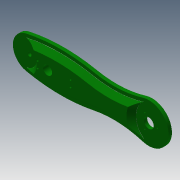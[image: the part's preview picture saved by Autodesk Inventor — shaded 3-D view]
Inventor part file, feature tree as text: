
AUTODESK INVENTOR PART (.ipt)
format: ipt  version: 2013 (Build 170138000, 138)  size: 261,120 bytes
history: native  units: mm
features: sketch x11, extrude x8, chamfer x1
ambient origin geometry x8: Origin, YZ Plane, XZ Plane, XY Plane, X Axis, Y Axis, Z Axis, Center Point
bodies: Solid1 (feature_tree)
feature tree (20):
  extrude  "Extrusion1"  Depth=50.0mm
  extrude  "Extrusion2"  Depth=15.0mm
  extrude  "Extrusion3"  Depth=5.0mm TaperAngle=0.0deg
  extrude  "Extrusion4"  Depth=18.1mm
  extrude  "Extrusion5"  Depth=20.0mm
  extrude  "Extrusion6"  Depth=9.5mm
  sketch  "Sketch7"  dims[d15=9.9mm d16=9.5mm]
  extrude  "Extrusion7"  Depth=9.5mm
  extrude  "Extrusion13"  Depth=3.0mm
  sketch  "Sketch15"  dims[d20=3.0mm]
  chamfer  "Chamfer2"  Distance=13.6mm
  sketch  "Sketch16"  dims[d21=3.0mm d22=13.6mm d23=5.0mm d24=0.0mm d26=2.0mm d29=2.0mm d30=2.0mm d31=5.0mm d32=0.0mm d63=5.0mm d64=0.0mm d65=5.0mm d66=0.0mm d72=20.0mm d73=30.0mm d74=7.3mm d75=0.0mm d103=6.0mm d104=5.0mm d105=0.0mm d106=7.0mm d107=2.0mm d108=45.0deg]
  sketch  "Sketch1"  dims[d0=180.0mm d1=50.0mm]
  sketch  "Sketch2"  dims[d2=5.0mm d3=0.0mm d4=15.0mm]
  sketch  "Sketch3"  dims[d5=15.0mm d6=5.0mm d7=0.0mm]
  sketch  "Sketch4"  dims[d9=34.65mm d10=18.1mm]
  sketch  "Sketch5"  dims[d11=55.0mm d12=20.0mm]
  sketch  "Sketch6"  dims[d13=40.2mm d14=9.5mm]
  sketch  "Sketch8"  dims[d17=9.9mm d18=3.0mm]
  sketch  "Sketch14"  dims[d19=3.0mm]
